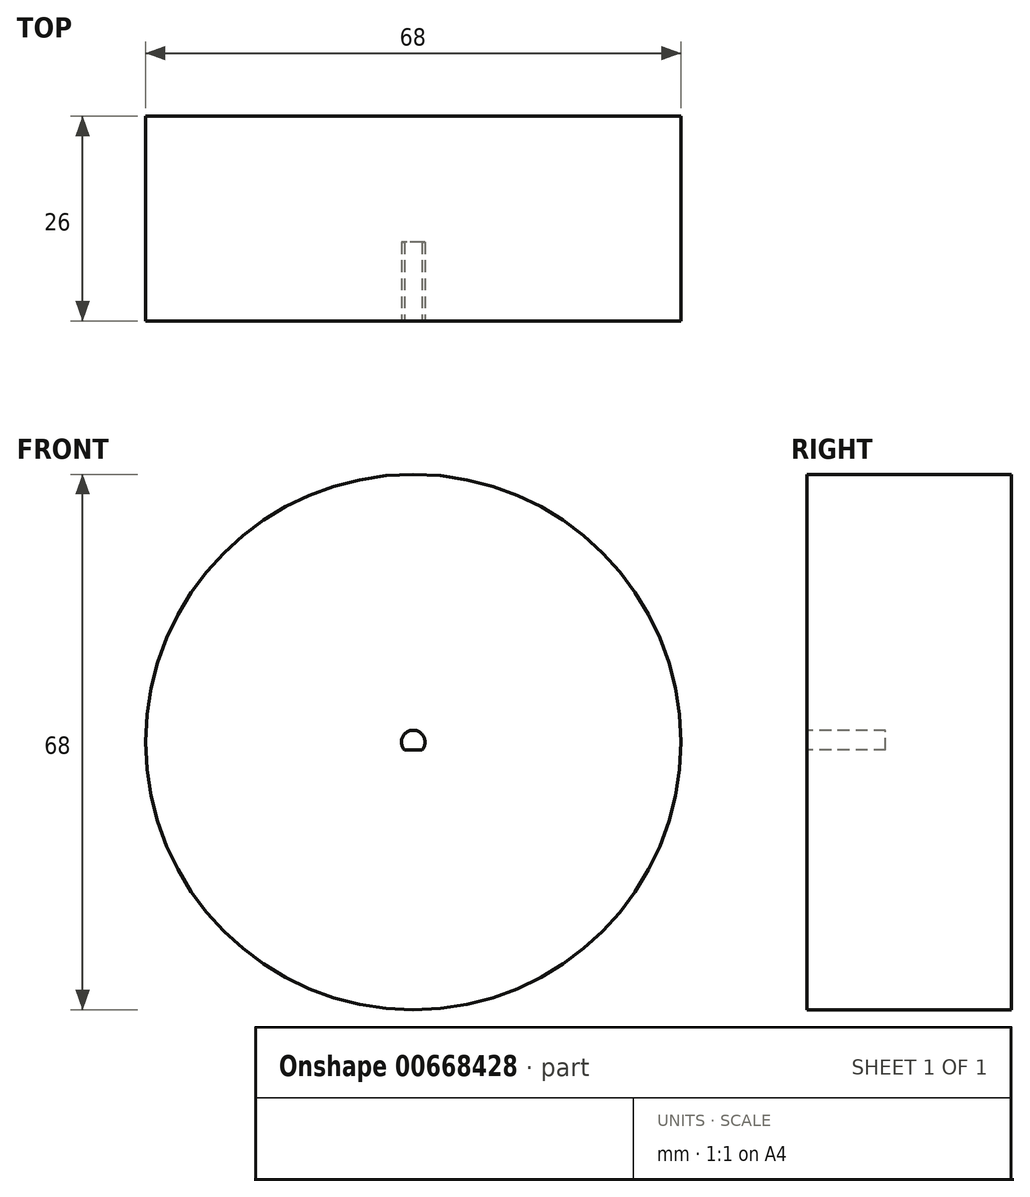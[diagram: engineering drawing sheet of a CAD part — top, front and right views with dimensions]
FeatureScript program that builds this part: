
annotation { "Feature Type Name" : "Feature", "Feature Type Description" : "" }
export const myFeature = defineFeature(function(context is Context, id is Id, definition is map)
    precondition{}
    {
        {
            var Q0;
            Q0=qCreatedBy(makeId("Front.planeOp"),FACE);
            var sketch = newSketch(context, id + "F0", { "sketchPlane" : qUnion([Q0])});
            skCircle(sketch, "E0", {"center": v(0, 0) * mm, "radius": 34 * mm});
            skSolve(sketch);
        }
        {
            var Q0;
            Q0=makeQuery(id+"F0.imprint","IMPRINT",FACE,{"disambiguationData":[TD([[makeQuery(id+"F0.imprint","IMPRINT",EDGE,{"derivedFrom":sQuery(id+"F0.wireOp",EDGE,"E0")}),1.0]])]});
            extrude(context, id + "F1", {"entities" : qUnion([Q0]), "depth" : 26 * mm, "offsetDistance" : 25 * mm});
        }
        {
            var Q0;
            Q0=makeQuery(id+"F1.opExtrude","CAP_FACE",FACE,{"disambiguationData":[OSD([sQuery(id+"F0.wireOp",EDGE,"E0")])],"isStart":false});
            var sketch = newSketch(context, id + "F2", { "sketchPlane" : qUnion([Q0])});
            skCircle(sketch, "E1", {"center": v(0, 0) * mm, "radius": 1.5 * mm});
            skLineSegment(sketch, "E2", {"start": v(0, 1.5) * mm, "end": v(0, -1) * mm});
            skLineSegment(sketch, "E3", {"start": v(0, -1) * mm, "end": v(1.12, -1) * mm});
            skLineSegment(sketch, "E4", {"start": v(1.12, -1) * mm, "end": v(-1.12, -1) * mm});
            skSolve(sketch);
        }
        {
            var Q0;
            {var subQ0=sQuery(id+"F2.wireOp",EDGE,"E2");Q0=makeQuery(id+"F2.imprint","IMPRINT",FACE,{"disambiguationData":[TD([[makeQuery(id+"F2.imprint","IMPRINT",EDGE,{"derivedFrom":subQ0}),-1.0]])]});}
            var Q1;
            {var subQ0=sQuery(id+"F2.wireOp",EDGE,"E2");Q1=makeQuery(id+"F2.imprint","IMPRINT",FACE,{"disambiguationData":[TD([[makeQuery(id+"F2.imprint","IMPRINT",EDGE,{"derivedFrom":subQ0}),1.0]])]});}
            extrude(context, id + "F3", {"entities" : qUnion([Q0, Q1]), "operationType" : NewBodyOperationType.REMOVE, "oppositeDirection" : true, "depth" : 10 * mm, "offsetDistance" : 25 * mm});
        }
    });
